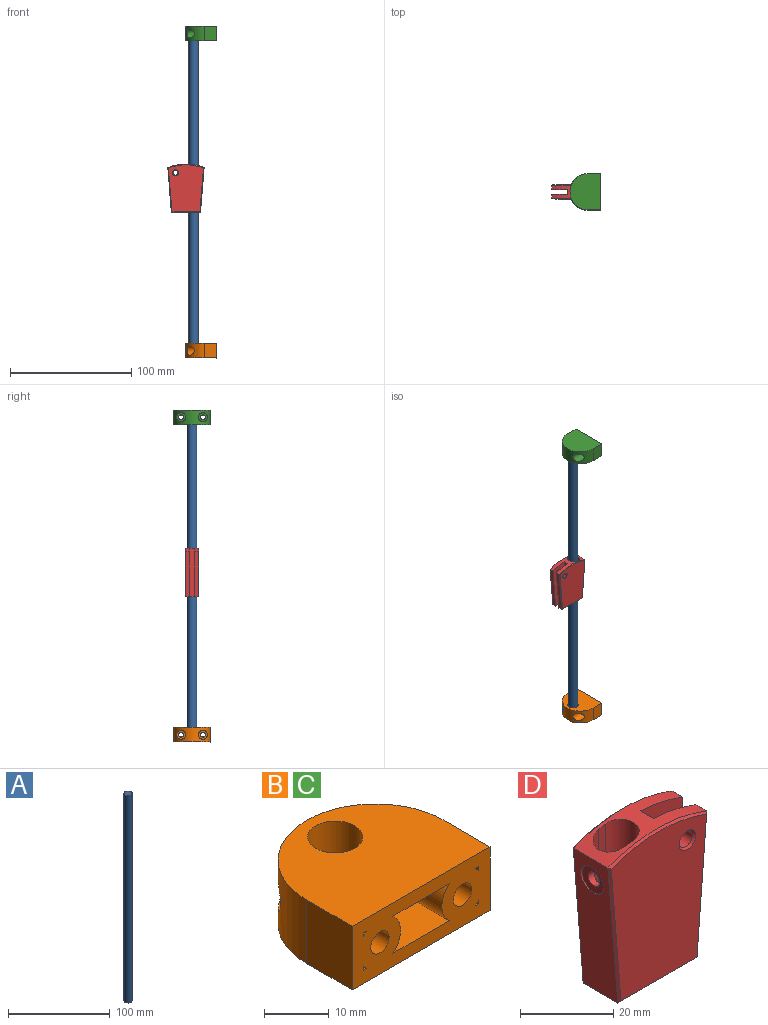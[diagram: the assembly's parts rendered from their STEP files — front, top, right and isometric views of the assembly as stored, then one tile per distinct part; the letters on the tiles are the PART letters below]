
ASSEMBLY  parts=4 mates=4
PART A: 3 faces, bbox 8x8x250 mm
  f0: cylinder r=4mm len=250mm, axis (0,0,-1), area 6283.2mm2, adj f1,f2
  f1: plane 8x8mm, normal (0,0,1), area 50.3mm2, adj f0
  f2: plane 8x8mm, normal (0,0,-1), area 50.3mm2, adj f0
PART B: 39 faces, bbox 30x25x12 mm
  f0: plane 30x12mm, normal (0,-1,0), area 263.9mm2, adj f2,f3,f4,f5,f8,f9,f15,f16
  f1: cylinder r=15mm len=30mm, axis (0,0,-1), area 452.6mm2, adj f2,f3,f4,f5,f11,f12
  f2: plane 12x10mm, normal (-1,0,0), area 120mm2, adj f0,f1,f4,f5
  f3: plane 12x10mm, normal (1,0,0), area 120mm2, adj f0,f1,f4,f5
  f4: plane 30x25mm, normal (0,0,1), area 596.7mm2, adj f0,f1,f2,f3,f6
  f5: plane 30x25mm, normal (0,0,-1), area 653.4mm2, adj f0,f1,f2,f3
  f6: cylinder r=4.25mm len=10mm, axis (0,0,1), area 267mm2, adj f4,f7
  f7: plane 8.5x8.5mm, normal (0,0,1), area 56.7mm2, adj f6
  f8: cylinder r=2mm len=10mm, axis (0,-1,0), area 125.7mm2, adj f0,f13
  f9: cylinder r=2mm len=10mm, axis (0,-1,0), area 125.7mm2, adj f0,f10
  f10: plane 7.44x7.44mm, normal (0,1,0), area 30.9mm2, adj f9,f11
  f11: cylinder r=3.72mm len=14.04mm, axis (0,-1,0), area 269mm2, adj f1,f10
  f12: cylinder r=3.72mm len=14.04mm, axis (0,-1,0), area 269.1mm2, adj f1,f13
  f13: plane 7.44x7.44mm, normal (0,1,0), area 30.9mm2, adj f8,f12
  f14: plane 0.67x0.67mm, normal (0,-1,0), area 0.2mm2, adj f15,f16,f17
  f15: cylinder r=4.5mm len=7.5mm, axis (0,-1,0), area 7.1mm2, adj f0,f14,f16,f17
  f16: plane 7.5x0.67mm, normal (0,0,1), area 5mm2, adj f0,f14,f15,f17
  f17: plane 7.5x0.67mm, normal (-1,0,0), area 5mm2, adj f0,f14,f15,f16
  f18: cylinder r=4.5mm len=7.5mm, axis (0,-1,0), area 7.1mm2, adj f0,f19,f20,f21
  f19: plane 7.5x0.67mm, normal (1,0,0), area 5mm2, adj f0,f18,f20,f21
  f20: plane 7.5x0.67mm, normal (0,0,-1), area 5mm2, adj f0,f18,f19,f21
  f21: plane 0.67x0.67mm, normal (0,-1,0), area 0.2mm2, adj f18,f19,f20
  f22: cylinder r=6.22mm len=7mm, axis (0,-1,0), area 39.3mm2, adj f25,f26,f28,f29
  f23: cylinder r=4.5mm len=7.5mm, axis (0,-1,0), area 60.2mm2, adj f0,f25,f26,f28
  f24: cylinder r=4.5mm len=7.5mm, axis (0,-1,0), area 60.2mm2, adj f0,f25,f28,f30
  f25: plane 13.21x12.34mm, normal (0,0,1), area 130.3mm2, adj f0,f22,f23,f24,f26,f27,f29,f30
  f26: plane 7x3.39mm, normal (0,-1,0), area 13.2mm2, adj f22,f23,f25,f28
  f27: cylinder r=6.22mm len=7mm, axis (0,-1,0), area 39.3mm2, adj f25,f28,f29,f30
  f28: plane 13.21x12.34mm, normal (0,0,-1), area 130.3mm2, adj f0,f22,f23,f24,f26,f27,f29,f30
  f29: cylinder r=6.75mm len=7.72mm, axis (0,0,1), area 45.6mm2, adj f22,f25,f27,f28
  f30: plane 7x3.39mm, normal (0,-1,0), area 13.2mm2, adj f24,f25,f27,f28
  f31: plane 7.5x0.67mm, normal (1,0,0), area 5mm2, adj f0,f32,f33,f34
  f32: plane 7.5x0.67mm, normal (0,0,1), area 5mm2, adj f0,f31,f33,f34
  f33: cylinder r=4.5mm len=7.5mm, axis (0,-1,0), area 7.1mm2, adj f0,f31,f32,f34
  f34: plane 0.67x0.67mm, normal (0,-1,0), area 0.2mm2, adj f31,f32,f33
  f35: plane 7.5x0.67mm, normal (-1,0,0), area 5mm2, adj f0,f36,f37,f38
  f36: cylinder r=4.5mm len=7.5mm, axis (0,-1,0), area 7.1mm2, adj f0,f35,f37,f38
  f37: plane 0.67x0.67mm, normal (0,-1,0), area 0.2mm2, adj f35,f36,f38
  f38: plane 7.5x0.67mm, normal (0,0,-1), area 5mm2, adj f0,f35,f36,f37
PART C: same geometry as B
PART D: 30 faces, bbox 30x11.5x39.9 mm
  f0: plane 38.92x28.94mm, normal (0,-1,0), area 974.5mm2, adj f20,f21,f22,f23,f24
  f1: plane 38.92x28.94mm, normal (0,1,0), area 974.5mm2, adj f25,f26,f27,f28,f29
  f2: cylinder r=4.25mm len=39.87mm, axis (0,0,-1), area 797.6mm2, adj f3,f5,f9,f10,f18
  f3: plane 19.42x2mm, normal (0,-1,0), area 38.5mm2, adj f2,f4,f10,f18
  f4: cylinder r=4.25mm len=19.06mm, axis (0,0,1), area 235.3mm2, adj f3,f5,f10,f18,f19
  f5: plane 19.42x2mm, normal (0,1,0), area 38.5mm2, adj f2,f4,f10,f18
  f6: plane 39.87x4mm, normal (1,0,0), area 159.5mm2, adj f7,f8,f9,f18
  f7: plane 39.87x13mm, normal (0,-1,0), area 436.5mm2, adj f6,f9,f14,f15,f18
  f8: plane 39.87x13mm, normal (0,1,0), area 436.5mm2, adj f6,f9,f12,f13,f18
  f9: plane 24x10.5mm, normal (0,0,-1), area 155.3mm2, adj f2,f6,f7,f8,f11,f12,f14,f23
  f10: plane 8.5x6.25mm, normal (0,0,1), area 17mm2, adj f2,f3,f4,f5
  f11: plane 36.99x10.5mm, normal (-1,0,-0.08), area 351.1mm2, adj f9,f17,f18,f22,f25
  f12: plane 36.99x3.25mm, normal (1,0,-0.08), area 120.6mm2, adj f8,f9,f18,f21
  f13: cylinder r=2mm len=4mm, axis (0,-1,0), area 40.8mm2, adj f8,f24
  f14: plane 36.99x3.25mm, normal (1,0,-0.08), area 120.6mm2, adj f7,f9,f18,f28
  f15: cylinder r=2mm len=4mm, axis (0,-1,0), area 40.8mm2, adj f7,f29
  f16: plane 7x7mm, normal (-1,0,0), area 28.9mm2, adj f17,f19
  f17: cylinder r=3.5mm len=7mm, axis (-1,0,0), area 11.2mm2, adj f11,f16
  f18: cylinder r=39.92mm len=30mm, axis (0,-1,0), area 194.3mm2, adj f2,f3,f4,f5,f6,f7,f8,f11
  f19: cylinder r=1.75mm len=3.5mm, axis (-1,0,0), area 18.5mm2, adj f4,f16
  f20: cone r=39.42mm half-angle=45deg, axis (0,1,0), area 21.4mm2, adj f0,f18,f21,f22
  f21: plane 36.99x3.46mm, normal (0.7,-0.71,-0.06), area 25.9mm2, adj f0,f12,f20,f23
  f22: plane 36.99x3.46mm, normal (-0.7,-0.71,-0.06), area 25.9mm2, adj f0,f11,f20,f23
  f23: plane 24x0.5mm, normal (0,-0.71,-0.71), area 16.6mm2, adj f0,f9,f21,f22
  f24: cone r=2mm half-angle=45deg, axis (0,-1,0), area 10mm2, adj f0,f13
  f25: plane 36.99x3.46mm, normal (-0.7,0.71,-0.06), area 25.9mm2, adj f1,f11,f26,f27
  f26: cone r=39.92mm half-angle=45deg, axis (0,-1,0), area 21.4mm2, adj f1,f18,f25,f28
  f27: plane 24x0.5mm, normal (0,0.71,-0.71), area 16.6mm2, adj f1,f9,f25,f28
  f28: plane 36.99x3.46mm, normal (0.7,0.71,-0.06), area 25.9mm2, adj f1,f14,f26,f27
  f29: cone r=2.5mm half-angle=45deg, axis (0,1,0), area 10mm2, adj f1,f15
PLACE A rot(axis=(0,0,-1),180deg) t=(-79.32,-93,29.74)mm
PLACE B rot(axis=(0,0,1),90deg) t=(-70.57,-93,-107.26)mm
PLACE C rot(axis=(0.71,-0.71,0),180deg) t=(-70.57,-93,166.74)mm
PLACE D rot(axis=(0,0,-1),180deg) t=(-85.57,-93,12.78)mm
MATE revolute B.f6 <-> A.f0  axis (0,0,1) through (-79.32,-93,-95.26)mm
MATE revolute C.f6 <-> A.f0  axis (0,0,-1) through (-79.32,-93,154.74)mm
MATE slider D.f2 <-> A.f0  axis (0,0,-1) through (-79.32,-93,52.89)mm
MATE parallel B.f0 <-> C.f0  axis (1,0,0) through (-60.57,-78,-101.26)mm
